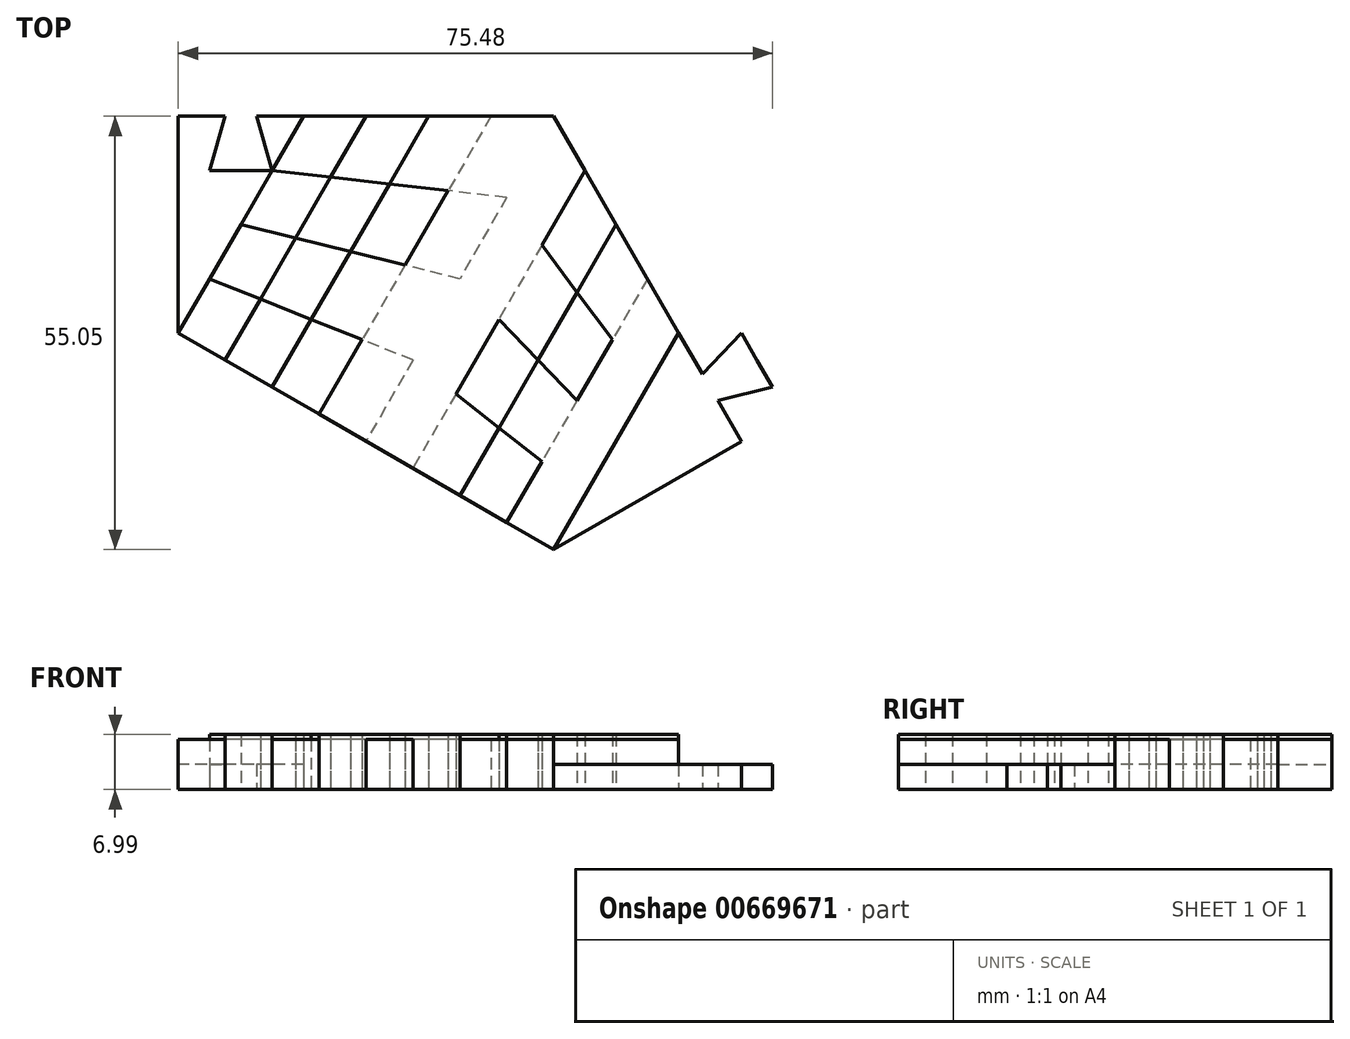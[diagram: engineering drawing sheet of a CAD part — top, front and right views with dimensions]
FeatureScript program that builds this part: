
annotation { "Feature Type Name" : "Feature", "Feature Type Description" : "" }
export const myFeature = defineFeature(function(context is Context, id is Id, definition is map)
    precondition{}
    {
        {
            var Q0;
            Q0=qCreatedBy(makeId("Top.planeOp"),FACE);
            var sketch = newSketch(context, id + "F0", { "sketchPlane" : qUnion([Q0])});
            skLineSegment(sketch, "E0.2", {"start": v(-124.16, -41.74) * mm, "end": v(-171.83, -14.22) * mm});
            skLineSegment(sketch, "E1", {"start": v(-124.16, 13.3) * mm, "end": v(-148, -27.98) * mm});
            skLineSegment(sketch, "E2", {"start": v(-124.16, 13.3) * mm, "end": v(-100.32, -27.98) * mm});
            skLineSegment(sketch, "E3", {"start": v(-124.16, -41.74) * mm, "end": v(-108.27, -14.22) * mm});
            skLineSegment(sketch, "E4", {"start": v(-155.94, 13.3) * mm, "end": v(-171.83, -14.22) * mm});
            skLineSegment(sketch, "E5", {"start": v(-116.21, -27.98) * mm, "end": v(-136.08, -7.34) * mm});
            skLineSegment(sketch, "E6", {"start": v(-136.08, -7.34) * mm, "end": v(-163.89, -0.46) * mm});
            skLineSegment(sketch, "E7", {"start": v(-116.21, -27.98) * mm, "end": v(-124.16, -41.74) * mm});
            skLineSegment(sketch, "E8", {"start": v(-136.08, -7.34) * mm, "end": v(-148, -27.98) * mm});
            skLineSegment(sketch, "E9", {"start": v(-163.89, -0.46) * mm, "end": v(-171.83, -14.22) * mm});
            skLineSegment(sketch, "E10", {"start": v(-120.18, -34.86) * mm, "end": v(-142.04, -17.66) * mm});
            skLineSegment(sketch, "E11", {"start": v(-142.04, -17.66) * mm, "end": v(-167.86, -7.34) * mm});
            skLineSegment(sketch, "E12", {"start": v(-116.21, -27.98) * mm, "end": v(-108.27, -14.22) * mm});
            skLineSegment(sketch, "E13", {"start": v(-124.16, 13.3) * mm, "end": v(-136.08, -7.34) * mm});
            skLineSegment(sketch, "E14", {"start": v(-155.94, 13.3) * mm, "end": v(-163.89, -0.46) * mm});
            skLineSegment(sketch, "E15", {"start": v(-112.24, -21.1) * mm, "end": v(-130.12, 2.99) * mm});
            skLineSegment(sketch, "E16", {"start": v(-130.12, 2.99) * mm, "end": v(-159.91, 6.43) * mm});
            skLineSegment(sketch, "E17", {"start": v(-148, -27.98) * mm, "end": v(-136.08, -34.86) * mm});
            skLineSegment(sketch, "E18", {"start": v(-136.08, -34.86) * mm, "end": v(-124.16, -41.74) * mm});
            skLineSegment(sketch, "E19", {"start": v(-148, -27.98) * mm, "end": v(-159.91, -21.1) * mm});
            skLineSegment(sketch, "E20", {"start": v(-171.83, -14.22) * mm, "end": v(-159.91, -21.1) * mm});
            skLineSegment(sketch, "E21", {"start": v(-132.1, 13.3) * mm, "end": v(-153.95, -24.54) * mm});
            skLineSegment(sketch, "E22", {"start": v(-140.05, 13.3) * mm, "end": v(-159.91, -21.1) * mm});
            skLineSegment(sketch, "E23", {"start": v(-148, 13.3) * mm, "end": v(-165.87, -17.66) * mm});
            skLineSegment(sketch, "E24", {"start": v(-124.16, 13.3) * mm, "end": v(-108.27, -14.22) * mm});
            skLineSegment(sketch, "E25", {"start": v(-116.21, -0.46) * mm, "end": v(-124.16, 13.3) * mm});
            skLineSegment(sketch, "E26", {"start": v(-112.24, -7.34) * mm, "end": v(-130.12, -38.3) * mm});
            skLineSegment(sketch, "E27", {"start": v(-116.21, -0.46) * mm, "end": v(-136.08, -34.86) * mm});
            skLineSegment(sketch, "E28", {"start": v(-120.18, 6.43) * mm, "end": v(-142.04, -31.42) * mm});
            skLineSegment(sketch, "E29", {"start": v(-124.16, 13.3) * mm, "end": v(-171.83, 13.3) * mm});
            skLineSegment(sketch, "E30", {"start": v(-171.83, 13.3) * mm, "end": v(-171.83, -14.22) * mm});
            skLineSegment(sketch, "E31", {"start": v(-167.86, -7.34) * mm, "end": v(-167.86, 13.3) * mm});
            skLineSegment(sketch, "E32", {"start": v(-163.89, 13.3) * mm, "end": v(-163.89, -0.46) * mm});
            skLineSegment(sketch, "E33", {"start": v(-159.91, 13.3) * mm, "end": v(-159.91, 6.43) * mm});
            skLineSegment(sketch, "E34", {"start": v(-100.32, -27.98) * mm, "end": v(-124.16, -41.74) * mm});
            skLineSegment(sketch, "E35", {"start": v(-120.18, -34.86) * mm, "end": v(-102.32, -24.47) * mm});
            skLineSegment(sketch, "E36", {"start": v(-104.28, -21.17) * mm, "end": v(-116.21, -27.98) * mm});
            skLineSegment(sketch, "E37", {"start": v(-106.3, -17.67) * mm, "end": v(-112.24, -21.1) * mm});
            skLineSegment(sketch, "E38", {"start": v(-167.86, 13.3) * mm, "end": v(-171.83, 13.3) * mm});
            skLineSegment(sketch, "E39", {"start": v(-163.89, 13.3) * mm, "end": v(-167.86, 13.3) * mm});
            skLineSegment(sketch, "E40", {"start": v(-159.91, 13.3) * mm, "end": v(-163.89, 13.3) * mm});
            skLineSegment(sketch, "E41", {"start": v(-155.94, 13.3) * mm, "end": v(-159.91, 13.3) * mm});
            skLineSegment(sketch, "E42", {"start": v(-167.86, 13.3) * mm, "end": v(-167.86, -7.34) * mm});
            skLineSegment(sketch, "E43", {"start": v(-163.89, 6.43) * mm, "end": v(-167.86, 6.43) * mm});
            skLineSegment(sketch, "E44", {"start": v(-167.86, 6.43) * mm, "end": v(-165.87, 13.3) * mm});
            skLineSegment(sketch, "E45", {"start": v(-163.89, 6.43) * mm, "end": v(-159.91, 6.43) * mm});
            skLineSegment(sketch, "E46", {"start": v(-159.91, 6.43) * mm, "end": v(-161.9, 13.3) * mm});
            skLineSegment(sketch, "E47", {"start": v(-104.28, -21.17) * mm, "end": v(-98.31, -17.73) * mm});
            skLineSegment(sketch, "E48", {"start": v(-104.28, -21.17) * mm, "end": v(-106.3, -17.67) * mm});
            skLineSegment(sketch, "E49", {"start": v(-102.32, -24.47) * mm, "end": v(-104.28, -21.17) * mm});
            skLineSegment(sketch, "E50", {"start": v(-103.3, -22.82) * mm, "end": v(-96.35, -21.1) * mm});
            skLineSegment(sketch, "E51", {"start": v(-105.29, -19.42) * mm, "end": v(-100.32, -14.26) * mm});
            skLineSegment(sketch, "E52", {"start": v(-100.32, -14.26) * mm, "end": v(-98.31, -17.73) * mm});
            skLineSegment(sketch, "E53", {"start": v(-96.35, -21.1) * mm, "end": v(-98.31, -17.73) * mm});
            skSolve(sketch);
        }
        {
            var Q0;
            {var subQ3=sQuery(id+"F0.wireOp",EDGE,"E30");Q0=makeQuery(id+"F0.imprint","IMPRINT",FACE,{"disambiguationData":[TD([[makeQuery(id+"F0.imprint","IMPRINT",EDGE,{"derivedFrom":subQ3}),1.0]])]});}
            var Q1;
            {var subQ3=sQuery(id+"F0.wireOp",EDGE,"E44");Q1=makeQuery(id+"F0.imprint","IMPRINT",FACE,{"disambiguationData":[TD([[makeQuery(id+"F0.imprint","IMPRINT",EDGE,{"derivedFrom":subQ3}),1.0]])]});}
            var Q2;
            {var subQ5=sQuery(id+"F0.wireOp",EDGE,"E43");Q2=makeQuery(id+"F0.imprint","IMPRINT",FACE,{"disambiguationData":[TD([[makeQuery(id+"F0.imprint","IMPRINT",EDGE,{"derivedFrom":subQ5}),1.0]])]});}
            var Q3;
            {var subQ3=sQuery(id+"F0.wireOp",EDGE,"E45");Q3=makeQuery(id+"F0.imprint","IMPRINT",FACE,{"disambiguationData":[TD([[makeQuery(id+"F0.imprint","IMPRINT",EDGE,{"derivedFrom":subQ3}),-1.0]])]});}
            var Q4;
            {var subQ0=sQuery(id+"F0.wireOp",EDGE,"E33");Q4=makeQuery(id+"F0.imprint","IMPRINT",FACE,{"disambiguationData":[TD([[makeQuery(id+"F0.imprint","IMPRINT",EDGE,{"derivedFrom":subQ0}),-1.0]])]});}
            var Q5;
            {var subQ2=sQuery(id+"F0.wireOp",EDGE,"E33");Q5=makeQuery(id+"F0.imprint","IMPRINT",FACE,{"disambiguationData":[TD([[makeQuery(id+"F0.imprint","IMPRINT",EDGE,{"derivedFrom":subQ2}),1.0]])]});}
            var Q6;
            {var subQ0=sQuery(id+"F0.wireOp",EDGE,"E34");Q6=makeQuery(id+"F0.imprint","IMPRINT",FACE,{"disambiguationData":[TD([[makeQuery(id+"F0.imprint","IMPRINT",EDGE,{"derivedFrom":subQ0}),-1.0]])]});}
            var Q7;
            {var subQ0=sQuery(id+"F0.wireOp",EDGE,"E36");Q7=makeQuery(id+"F0.imprint","IMPRINT",FACE,{"disambiguationData":[TD([[makeQuery(id+"F0.imprint","IMPRINT",EDGE,{"derivedFrom":subQ0}),1.0]])]});}
            var Q8;
            {var subQ1=sQuery(id+"F0.wireOp",EDGE,"E36");Q8=makeQuery(id+"F0.imprint","IMPRINT",FACE,{"disambiguationData":[TD([[makeQuery(id+"F0.imprint","IMPRINT",EDGE,{"derivedFrom":subQ1}),-1.0]])]});}
            var Q9;
            {var subQ0=sQuery(id+"F0.wireOp",EDGE,"E37");Q9=makeQuery(id+"F0.imprint","IMPRINT",FACE,{"disambiguationData":[TD([[makeQuery(id+"F0.imprint","IMPRINT",EDGE,{"derivedFrom":subQ0}),-1.0]])]});}
            var Q10;
            {var subQ5=sQuery(id+"F0.wireOp",EDGE,"E52");Q10=makeQuery(id+"F0.imprint","IMPRINT",FACE,{"disambiguationData":[TD([[makeQuery(id+"F0.imprint","IMPRINT",EDGE,{"derivedFrom":subQ5}),-1.0]])]});}
            var Q11;
            {var subQ0=sQuery(id+"F0.wireOp",EDGE,"E50");Q11=makeQuery(id+"F0.imprint","IMPRINT",FACE,{"disambiguationData":[TD([[makeQuery(id+"F0.imprint","IMPRINT",EDGE,{"derivedFrom":subQ0}),1.0]])]});}
            var Q12;
            {var subQ0=sQuery(id+"F0.wireOp",EDGE,"E51");var subQ1=sQuery(id+"F0.wireOp",EDGE,"E2");var subQ2=makeQuery(id+"F0.imprint","INTERSECT",VERTEX,{"derivedFrom":[subQ1,subQ0]});Q12=makeQuery(id+"F0.imprint","IMPRINT",FACE,{"disambiguationData":[TD([[makeQuery(id+"F0.imprint","IMPRINT",EDGE,{"disambiguationData":[TD([[subQ2,-1.0]])],"derivedFrom":subQ1}),-1.0]])]});}
            var Q13;
            {var subQ1=sQuery(id+"F0.wireOp",EDGE,"E2");var subQ3=sQuery(id+"F0.wireOp",EDGE,"E47");var subQ4=makeQuery(id+"F0.imprint","INTERSECT",VERTEX,{"derivedFrom":[subQ1,subQ3]});Q13=makeQuery(id+"F0.imprint","IMPRINT",FACE,{"disambiguationData":[TD([[makeQuery(id+"F0.imprint","IMPRINT",EDGE,{"disambiguationData":[TD([[subQ4,-1.0]])],"derivedFrom":subQ1}),-1.0]])]});}
            extrude(context, id + "F1", {"entities" : qUnion([Q0, Q1, Q2, Q3, Q4, Q5, Q6, Q7, Q8, Q9, Q10, Q11, Q12, Q13]), "depth" : 3.17 * mm, "offsetDistance" : 25.4 * mm});
        }
        {
            var Q0;
            {var subQ0=sQuery(id+"F0.wireOp",EDGE,"E20");var subQ5=sQuery(id+"F0.wireOp",EDGE,"E23");var subQ7=makeQuery(id+"F0.imprint","INTERSECT",VERTEX,{"derivedFrom":[subQ0,subQ5]});Q0=makeQuery(id+"F0.imprint","IMPRINT",FACE,{"disambiguationData":[TD([[makeQuery(id+"F0.imprint","IMPRINT",EDGE,{"disambiguationData":[TD([[subQ7,1.0]])],"derivedFrom":subQ5}),-1.0]])]});}
            var Q1;
            {var subQ0=sQuery(id+"F0.wireOp",EDGE,"E22");var subQ1=sQuery(id+"F0.wireOp",EDGE,"E6");var subQ2=makeQuery(id+"F0.imprint","INTERSECT",VERTEX,{"derivedFrom":[subQ1,subQ0]});Q1=makeQuery(id+"F0.imprint","IMPRINT",FACE,{"disambiguationData":[TD([[makeQuery(id+"F0.imprint","IMPRINT",EDGE,{"disambiguationData":[TD([[subQ2,-1.0]])],"derivedFrom":subQ1}),1.0]])]});}
            var Q2;
            {var subQ0=sQuery(id+"F0.wireOp",EDGE,"E21");var subQ1=sQuery(id+"F0.wireOp",EDGE,"E11");var subQ2=makeQuery(id+"F0.imprint","INTERSECT",VERTEX,{"derivedFrom":[subQ1,subQ0]});Q2=makeQuery(id+"F0.imprint","IMPRINT",FACE,{"disambiguationData":[TD([[makeQuery(id+"F0.imprint","IMPRINT",EDGE,{"disambiguationData":[TD([[subQ2,-1.0]])],"derivedFrom":subQ1}),1.0]])]});}
            var Q3;
            {var subQ1=sQuery(id+"F0.wireOp",EDGE,"E6");var subQ3=sQuery(id+"F0.wireOp",EDGE,"E21");var subQ4=makeQuery(id+"F0.imprint","INTERSECT",VERTEX,{"derivedFrom":[subQ1,subQ3]});Q3=makeQuery(id+"F0.imprint","IMPRINT",FACE,{"disambiguationData":[TD([[makeQuery(id+"F0.imprint","IMPRINT",EDGE,{"disambiguationData":[TD([[subQ4,-1.0]])],"derivedFrom":subQ3}),1.0]])]});}
            var Q4;
            {var subQ0=sQuery(id+"F0.wireOp",EDGE,"E17");var subQ5=sQuery(id+"F0.wireOp",EDGE,"E28");var subQ6=makeQuery(id+"F0.imprint","INTERSECT",VERTEX,{"derivedFrom":[subQ0,subQ5]});Q4=makeQuery(id+"F0.imprint","IMPRINT",FACE,{"disambiguationData":[TD([[makeQuery(id+"F0.imprint","IMPRINT",EDGE,{"disambiguationData":[TD([[subQ6,1.0]])],"derivedFrom":subQ5}),-1.0]])]});}
            var Q5;
            {var subQ0=sQuery(id+"F0.wireOp",EDGE,"E27");var subQ1=sQuery(id+"F0.wireOp",EDGE,"E5");var subQ2=makeQuery(id+"F0.imprint","INTERSECT",VERTEX,{"derivedFrom":[subQ1,subQ0]});Q5=makeQuery(id+"F0.imprint","IMPRINT",FACE,{"disambiguationData":[TD([[makeQuery(id+"F0.imprint","IMPRINT",EDGE,{"disambiguationData":[TD([[subQ2,-1.0]])],"derivedFrom":subQ1}),1.0]])]});}
            var Q6;
            {var subQ0=sQuery(id+"F0.wireOp",EDGE,"E26");var subQ1=sQuery(id+"F0.wireOp",EDGE,"E10");var subQ2=makeQuery(id+"F0.imprint","INTERSECT",VERTEX,{"derivedFrom":[subQ1,subQ0]});Q6=makeQuery(id+"F0.imprint","IMPRINT",FACE,{"disambiguationData":[TD([[makeQuery(id+"F0.imprint","IMPRINT",EDGE,{"disambiguationData":[TD([[subQ2,-1.0]])],"derivedFrom":subQ1}),1.0]])]});}
            var Q7;
            {var subQ1=sQuery(id+"F0.wireOp",EDGE,"E5");var subQ3=sQuery(id+"F0.wireOp",EDGE,"E26");var subQ4=makeQuery(id+"F0.imprint","INTERSECT",VERTEX,{"derivedFrom":[subQ1,subQ3]});Q7=makeQuery(id+"F0.imprint","IMPRINT",FACE,{"disambiguationData":[TD([[makeQuery(id+"F0.imprint","IMPRINT",EDGE,{"disambiguationData":[TD([[subQ4,-1.0]])],"derivedFrom":subQ3}),1.0]])]});}
            var Q8;
            {var subQ0=sQuery(id+"F0.wireOp",EDGE,"E26");var subQ1=sQuery(id+"F0.wireOp",EDGE,"E5");var subQ2=makeQuery(id+"F0.imprint","INTERSECT",VERTEX,{"derivedFrom":[subQ1,subQ0]});Q8=makeQuery(id+"F0.imprint","IMPRINT",FACE,{"disambiguationData":[TD([[makeQuery(id+"F0.imprint","IMPRINT",EDGE,{"disambiguationData":[TD([[subQ2,-1.0]])],"derivedFrom":subQ1}),-1.0]])]});}
            var Q9;
            {var subQ1=sQuery(id+"F0.wireOp",EDGE,"E6");var subQ3=sQuery(id+"F0.wireOp",EDGE,"E23");var subQ4=makeQuery(id+"F0.imprint","INTERSECT",VERTEX,{"derivedFrom":[subQ1,subQ3]});Q9=makeQuery(id+"F0.imprint","IMPRINT",FACE,{"disambiguationData":[TD([[makeQuery(id+"F0.imprint","IMPRINT",EDGE,{"disambiguationData":[TD([[subQ4,1.0]])],"derivedFrom":subQ3}),-1.0]])]});}
            var Q10;
            {var subQ0=sQuery(id+"F0.wireOp",EDGE,"E21");var subQ1=sQuery(id+"F0.wireOp",EDGE,"E6");var subQ2=makeQuery(id+"F0.imprint","INTERSECT",VERTEX,{"derivedFrom":[subQ1,subQ0]});Q10=makeQuery(id+"F0.imprint","IMPRINT",FACE,{"disambiguationData":[TD([[makeQuery(id+"F0.imprint","IMPRINT",EDGE,{"disambiguationData":[TD([[subQ2,-1.0]])],"derivedFrom":subQ1}),-1.0]])]});}
            var Q11;
            {var subQ1=sQuery(id+"F0.wireOp",EDGE,"E5");var subQ3=sQuery(id+"F0.wireOp",EDGE,"E28");var subQ4=makeQuery(id+"F0.imprint","INTERSECT",VERTEX,{"derivedFrom":[subQ1,subQ3]});Q11=makeQuery(id+"F0.imprint","IMPRINT",FACE,{"disambiguationData":[TD([[makeQuery(id+"F0.imprint","IMPRINT",EDGE,{"disambiguationData":[TD([[subQ4,1.0]])],"derivedFrom":subQ3}),-1.0]])]});}
            var Q12;
            {var subQ0=sQuery(id+"F0.wireOp",EDGE,"E22");var subQ1=sQuery(id+"F0.wireOp",EDGE,"E16");var subQ2=makeQuery(id+"F0.imprint","INTERSECT",VERTEX,{"derivedFrom":[subQ1,subQ0]});Q12=makeQuery(id+"F0.imprint","IMPRINT",FACE,{"disambiguationData":[TD([[makeQuery(id+"F0.imprint","IMPRINT",EDGE,{"disambiguationData":[TD([[subQ2,-1.0]])],"derivedFrom":subQ1}),-1.0]])]});}
            var Q13;
            {var subQ0=sQuery(id+"F0.wireOp",EDGE,"E29");var subQ5=sQuery(id+"F0.wireOp",EDGE,"E21");var subQ6=makeQuery(id+"F0.imprint","INTERSECT",VERTEX,{"derivedFrom":[subQ5,subQ0]});Q13=makeQuery(id+"F0.imprint","IMPRINT",FACE,{"disambiguationData":[TD([[makeQuery(id+"F0.imprint","IMPRINT",EDGE,{"disambiguationData":[TD([[subQ6,-1.0]])],"derivedFrom":subQ5}),1.0]])]});}
            var Q14;
            {var subQ0=sQuery(id+"F0.wireOp",EDGE,"E27");var subQ1=sQuery(id+"F0.wireOp",EDGE,"E15");var subQ2=makeQuery(id+"F0.imprint","INTERSECT",VERTEX,{"derivedFrom":[subQ1,subQ0]});Q14=makeQuery(id+"F0.imprint","IMPRINT",FACE,{"disambiguationData":[TD([[makeQuery(id+"F0.imprint","IMPRINT",EDGE,{"disambiguationData":[TD([[subQ2,-1.0]])],"derivedFrom":subQ1}),-1.0]])]});}
            var Q15;
            {var subQ0=sQuery(id+"F0.wireOp",EDGE,"E24");var subQ5=sQuery(id+"F0.wireOp",EDGE,"E26");var subQ7=makeQuery(id+"F0.imprint","INTERSECT",VERTEX,{"derivedFrom":[subQ0,subQ5]});Q15=makeQuery(id+"F0.imprint","IMPRINT",FACE,{"disambiguationData":[TD([[makeQuery(id+"F0.imprint","IMPRINT",EDGE,{"disambiguationData":[TD([[subQ7,-1.0]])],"derivedFrom":subQ5}),1.0]])]});}
            extrude(context, id + "F2", {"entities" : qUnion([Q0, Q1, Q2, Q3, Q4, Q5, Q6, Q7, Q8, Q9, Q10, Q11, Q12, Q13, Q14, Q15]), "depth" : 6.35 * mm, "offsetDistance" : 25.4 * mm});
        }
        {
            var Q0;
            {var subQ0=sQuery(id+"F0.wireOp",EDGE,"E29");var subQ5=sQuery(id+"F0.wireOp",EDGE,"E23");var subQ7=makeQuery(id+"F0.imprint","INTERSECT",VERTEX,{"derivedFrom":[subQ5,subQ0]});Q0=makeQuery(id+"F0.imprint","IMPRINT",FACE,{"disambiguationData":[TD([[makeQuery(id+"F0.imprint","IMPRINT",EDGE,{"disambiguationData":[TD([[subQ7,-1.0]])],"derivedFrom":subQ5}),-1.0]])]});}
            var Q1;
            {var subQ0=sQuery(id+"F0.wireOp",EDGE,"E22");var subQ1=sQuery(id+"F0.wireOp",EDGE,"E6");var subQ2=makeQuery(id+"F0.imprint","INTERSECT",VERTEX,{"derivedFrom":[subQ1,subQ0]});Q1=makeQuery(id+"F0.imprint","IMPRINT",FACE,{"disambiguationData":[TD([[makeQuery(id+"F0.imprint","IMPRINT",EDGE,{"disambiguationData":[TD([[subQ2,-1.0]])],"derivedFrom":subQ1}),-1.0]])]});}
            var Q2;
            {var subQ1=sQuery(id+"F0.wireOp",EDGE,"E6");var subQ3=sQuery(id+"F0.wireOp",EDGE,"E23");var subQ4=makeQuery(id+"F0.imprint","INTERSECT",VERTEX,{"derivedFrom":[subQ1,subQ3]});Q2=makeQuery(id+"F0.imprint","IMPRINT",FACE,{"disambiguationData":[TD([[makeQuery(id+"F0.imprint","IMPRINT",EDGE,{"disambiguationData":[TD([[subQ4,-1.0]])],"derivedFrom":subQ3}),-1.0]])]});}
            var Q3;
            {var subQ0=sQuery(id+"F0.wireOp",EDGE,"E22");var subQ1=sQuery(id+"F0.wireOp",EDGE,"E11");var subQ2=makeQuery(id+"F0.imprint","INTERSECT",VERTEX,{"derivedFrom":[subQ1,subQ0]});Q3=makeQuery(id+"F0.imprint","IMPRINT",FACE,{"disambiguationData":[TD([[makeQuery(id+"F0.imprint","IMPRINT",EDGE,{"disambiguationData":[TD([[subQ2,-1.0]])],"derivedFrom":subQ1}),1.0]])]});}
            var Q4;
            {var subQ0=sQuery(id+"F0.wireOp",EDGE,"E21");var subQ1=sQuery(id+"F0.wireOp",EDGE,"E6");var subQ2=makeQuery(id+"F0.imprint","INTERSECT",VERTEX,{"derivedFrom":[subQ1,subQ0]});Q4=makeQuery(id+"F0.imprint","IMPRINT",FACE,{"disambiguationData":[TD([[makeQuery(id+"F0.imprint","IMPRINT",EDGE,{"disambiguationData":[TD([[subQ2,-1.0]])],"derivedFrom":subQ1}),1.0]])]});}
            var Q5;
            {var subQ0=sQuery(id+"F0.wireOp",EDGE,"E19");var subQ5=sQuery(id+"F0.wireOp",EDGE,"E21");var subQ7=makeQuery(id+"F0.imprint","INTERSECT",VERTEX,{"derivedFrom":[subQ0,subQ5]});Q5=makeQuery(id+"F0.imprint","IMPRINT",FACE,{"disambiguationData":[TD([[makeQuery(id+"F0.imprint","IMPRINT",EDGE,{"disambiguationData":[TD([[subQ7,1.0]])],"derivedFrom":subQ5}),1.0]])]});}
            var Q6;
            {var subQ1=sQuery(id+"F0.wireOp",EDGE,"E5");var subQ3=sQuery(id+"F0.wireOp",EDGE,"E28");var subQ4=makeQuery(id+"F0.imprint","INTERSECT",VERTEX,{"derivedFrom":[subQ1,subQ3]});Q6=makeQuery(id+"F0.imprint","IMPRINT",FACE,{"disambiguationData":[TD([[makeQuery(id+"F0.imprint","IMPRINT",EDGE,{"disambiguationData":[TD([[subQ4,-1.0]])],"derivedFrom":subQ3}),-1.0]])]});}
            var Q7;
            {var subQ1=sQuery(id+"F0.wireOp",EDGE,"E6");var subQ3=sQuery(id+"F0.wireOp",EDGE,"E21");var subQ4=makeQuery(id+"F0.imprint","INTERSECT",VERTEX,{"derivedFrom":[subQ1,subQ3]});Q7=makeQuery(id+"F0.imprint","IMPRINT",FACE,{"disambiguationData":[TD([[makeQuery(id+"F0.imprint","IMPRINT",EDGE,{"disambiguationData":[TD([[subQ4,1.0]])],"derivedFrom":subQ3}),1.0]])]});}
            var Q8;
            {var subQ0=sQuery(id+"F0.wireOp",EDGE,"E21");var subQ1=sQuery(id+"F0.wireOp",EDGE,"E16");var subQ2=makeQuery(id+"F0.imprint","INTERSECT",VERTEX,{"derivedFrom":[subQ1,subQ0]});Q8=makeQuery(id+"F0.imprint","IMPRINT",FACE,{"disambiguationData":[TD([[makeQuery(id+"F0.imprint","IMPRINT",EDGE,{"disambiguationData":[TD([[subQ2,-1.0]])],"derivedFrom":subQ1}),-1.0]])]});}
            var Q9;
            {var subQ0=sQuery(id+"F0.wireOp",EDGE,"E25");var subQ5=sQuery(id+"F0.wireOp",EDGE,"E28");var subQ6=makeQuery(id+"F0.imprint","INTERSECT",VERTEX,{"derivedFrom":[subQ0,subQ5]});Q9=makeQuery(id+"F0.imprint","IMPRINT",FACE,{"disambiguationData":[TD([[makeQuery(id+"F0.imprint","IMPRINT",EDGE,{"disambiguationData":[TD([[subQ6,-1.0]])],"derivedFrom":subQ5}),-1.0]])]});}
            var Q10;
            {var subQ0=sQuery(id+"F0.wireOp",EDGE,"E27");var subQ1=sQuery(id+"F0.wireOp",EDGE,"E5");var subQ2=makeQuery(id+"F0.imprint","INTERSECT",VERTEX,{"derivedFrom":[subQ1,subQ0]});Q10=makeQuery(id+"F0.imprint","IMPRINT",FACE,{"disambiguationData":[TD([[makeQuery(id+"F0.imprint","IMPRINT",EDGE,{"disambiguationData":[TD([[subQ2,-1.0]])],"derivedFrom":subQ1}),-1.0]])]});}
            var Q11;
            {var subQ0=sQuery(id+"F0.wireOp",EDGE,"E27");var subQ1=sQuery(id+"F0.wireOp",EDGE,"E10");var subQ2=makeQuery(id+"F0.imprint","INTERSECT",VERTEX,{"derivedFrom":[subQ1,subQ0]});Q11=makeQuery(id+"F0.imprint","IMPRINT",FACE,{"disambiguationData":[TD([[makeQuery(id+"F0.imprint","IMPRINT",EDGE,{"disambiguationData":[TD([[subQ2,-1.0]])],"derivedFrom":subQ1}),1.0]])]});}
            var Q12;
            {var subQ0=sQuery(id+"F0.wireOp",EDGE,"E26");var subQ1=sQuery(id+"F0.wireOp",EDGE,"E5");var subQ2=makeQuery(id+"F0.imprint","INTERSECT",VERTEX,{"derivedFrom":[subQ1,subQ0]});Q12=makeQuery(id+"F0.imprint","IMPRINT",FACE,{"disambiguationData":[TD([[makeQuery(id+"F0.imprint","IMPRINT",EDGE,{"disambiguationData":[TD([[subQ2,-1.0]])],"derivedFrom":subQ1}),1.0]])]});}
            var Q13;
            {var subQ0=sQuery(id+"F0.wireOp",EDGE,"E26");var subQ1=sQuery(id+"F0.wireOp",EDGE,"E15");var subQ2=makeQuery(id+"F0.imprint","INTERSECT",VERTEX,{"derivedFrom":[subQ1,subQ0]});Q13=makeQuery(id+"F0.imprint","IMPRINT",FACE,{"disambiguationData":[TD([[makeQuery(id+"F0.imprint","IMPRINT",EDGE,{"disambiguationData":[TD([[subQ2,-1.0]])],"derivedFrom":subQ1}),-1.0]])]});}
            var Q14;
            {var subQ1=sQuery(id+"F0.wireOp",EDGE,"E5");var subQ3=sQuery(id+"F0.wireOp",EDGE,"E26");var subQ4=makeQuery(id+"F0.imprint","INTERSECT",VERTEX,{"derivedFrom":[subQ1,subQ3]});Q14=makeQuery(id+"F0.imprint","IMPRINT",FACE,{"disambiguationData":[TD([[makeQuery(id+"F0.imprint","IMPRINT",EDGE,{"disambiguationData":[TD([[subQ4,1.0]])],"derivedFrom":subQ3}),1.0]])]});}
            var Q15;
            {var subQ0=sQuery(id+"F0.wireOp",EDGE,"E18");var subQ5=sQuery(id+"F0.wireOp",EDGE,"E26");var subQ7=makeQuery(id+"F0.imprint","INTERSECT",VERTEX,{"derivedFrom":[subQ0,subQ5]});Q15=makeQuery(id+"F0.imprint","IMPRINT",FACE,{"disambiguationData":[TD([[makeQuery(id+"F0.imprint","IMPRINT",EDGE,{"disambiguationData":[TD([[subQ7,1.0]])],"derivedFrom":subQ5}),1.0]])]});}
            extrude(context, id + "F3", {"entities" : qUnion([Q0, Q1, Q2, Q3, Q4, Q5, Q6, Q7, Q8, Q9, Q10, Q11, Q12, Q13, Q14, Q15]), "depth" : 7 * mm, "offsetDistance" : 25.4 * mm});
        }
    });
